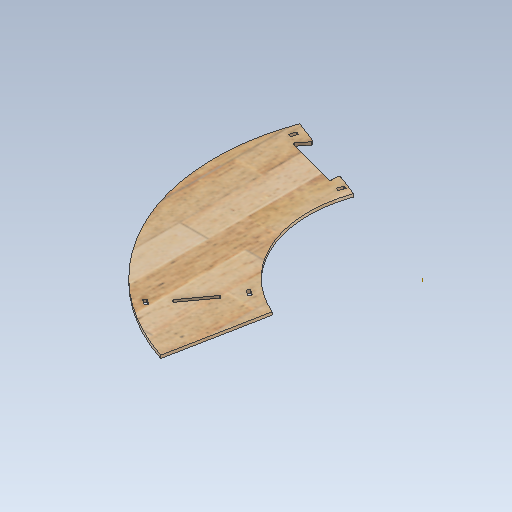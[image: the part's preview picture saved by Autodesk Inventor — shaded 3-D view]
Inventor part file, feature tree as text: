
AUTODESK INVENTOR PART (.ipt)
format: ipt  version: 2020 (Build 240168000, 168)  size: 461,824 bytes
history: native  units: mm
features: extrude x5, sketch x4, pattern_circular x3, mirror x2
ambient origin geometry x8: Origin, YZ Plane, XZ Plane, XY Plane, X Axis, Y Axis, Z Axis, Center Point
bodies: Body1 (feature_tree)
feature tree (14):
  extrude  "Extrusion3"  Depth=6.5mm
  extrude  "Extrusion4"  Depth=2.666667mm
  sketch  "Sketch3"  dims[d24=2.666667mm d25=2.666667mm]
  sketch  "Sketch5"  dims[d32=1.333333mm d33=1.333333mm]
  extrude  "Extrusion7"  Depth=1.333333mm
  pattern_circular  "Circular Pattern2"  [2 undecoded]
  pattern_circular  "Circular Pattern3"  [2 undecoded]
  mirror  "Mirror3"
  extrude  "Extrusion10"  Depth=0.5mm
  mirror  "Mirror4"
  pattern_circular  "Circular Pattern4"  [2 undecoded]
  extrude  "Extrusion11"  Depth=2.666667mm
  sketch  "Sketch2"  dims[d15=6.0mm d16=0.0mm d21=6.5mm]
  sketch  "Sketch6"  dims[d38=0.0mm d39=0.0mm d40=3.25mm d52=4.363323mm d60=0.872665mm d61=12.566371mm d62=13.439035mm d63=2.666667mm d64=0.523599mm d66=0.523599mm d67=2.666667mm d68=2.666667mm d70=12.566371mm d71=12.566371mm d84=467.42mm d85=850.0mm d86=658.71mm d87=150.07mm d88=425.0mm d89=4.363323mm d90=1.919862mm d91=1.919862mm d104=6.5mm d105=12.0mm d108=1.333333mm d109=1.333333mm d110=1.333333mm d111=1.333333mm d112=0.0mm d113=0.0mm d114=0.0mm d145=20.0mm d146=12.566371mm d149=145.0mm d150=90.0deg d151=90.0deg d152=90.0deg d153=90.0deg d154=20.0mm d155=25.132741mm d157=10.0mm d158=0.0mm d162=70.0mm d163=294.355mm d165=3.25mm d174=20.0mm d175=25.132741mm d177=0.0mm d178=0.0mm d176=0.5mm]
note: 6 required parameter values undecoded (feature->parameter linkage not recoverable at this tier; creation-order binding heuristic only, values carry confidence <= 0.55)
